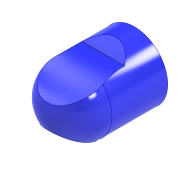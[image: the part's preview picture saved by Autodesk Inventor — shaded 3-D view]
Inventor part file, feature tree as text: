
AUTODESK INVENTOR PART (.ipt)
format: ipt  version: 2020 (Build 240168000, 168)  size: 578,048 bytes
history: native  units: mm
features: sketch x5, extrude x3, revolve x2, other x2, direct_edit x1
ambient origin geometry x8: Origin, YZ Plane, XZ Plane, XY Plane, X Axis, Y Axis, Z Axis, Center Point
bodies: Solid1 (feature_tree)
feature tree (13):
  extrude  "Extrusion1"  Depth=11.315mm TaperAngle=0.0deg
  revolve  "Revolution1"  [1 undecoded]
  extrude  "Extrusion2"  Depth=1.45mm
  revolve  "Revolution2"  [1 undecoded]
  direct_edit  "Direct Edit1"
  extrude  "Extrusion3"  Depth=10.0mm
  sketch  "Sketch1"  dims[d0=13.5mm d1=11.315mm d2=0.0mm]
  sketch  "Sketch2"  dims[d3=90.0deg d55=15.315mm d56=0.0mm]
  sketch  "Sketch3"  dims[d57=4.875mm d58=1.45mm]
  other  "Image1"
  sketch  "Sketch4"  dims[d59=0.685mm d60=1.5mm]
  sketch  "Sketch5"  dims[d61=1.2847mm d63=14.3mm d64=3.1075mm d65=90.0deg d66=8.0mm d67=10.0mm d68=10.0mm d69=2.0mm d70=0.0mm]
  other  "Scale1"
note: 2 required parameter values undecoded (feature->parameter linkage not recoverable at this tier; creation-order binding heuristic only, values carry confidence <= 0.55)
